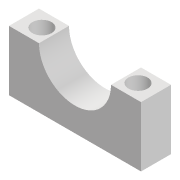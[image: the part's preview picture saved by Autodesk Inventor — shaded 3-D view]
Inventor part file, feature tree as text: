
AUTODESK INVENTOR PART (.ipt)
format: ipt  version: 2022 (Build 260153000, 153)  size: 108,544 bytes
history: native  units: mm
features: extrude x2, sketch x2
ambient origin geometry x8: Origin, YZ Plane, XZ Plane, XY Plane, X Axis, Y Axis, Z Axis, Center Point
bodies: Solid1 (feature_tree)
feature tree (4):
  extrude  "Extrusion1"  Depth=11.0mm
  extrude  "Extrusion2"  Depth=10.0mm
  sketch  "Sketch2"  dims[d0=12.0mm d1=11.0mm]
  sketch  "Sketch3"  dims[d2=11.0mm d3=10.0mm d4=3.0mm d5=5.0mm d6=0.0mm d7=3.2mm d8=3.0mm d9=2.5mm d10=3.2mm d11=3.0mm d12=2.5mm d13=10.0mm d14=0.0mm]
